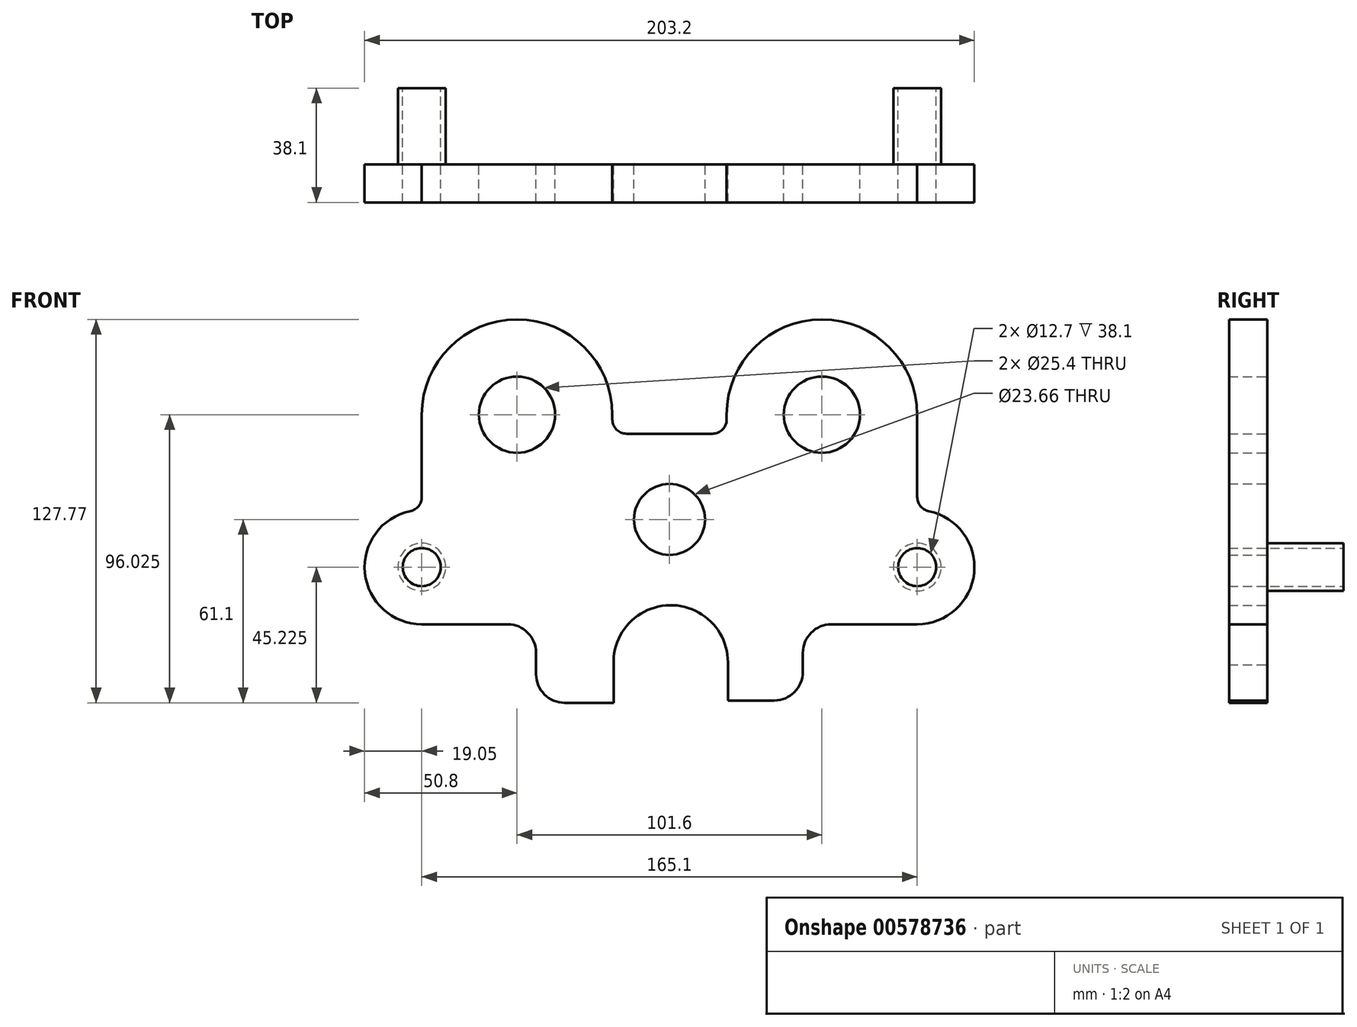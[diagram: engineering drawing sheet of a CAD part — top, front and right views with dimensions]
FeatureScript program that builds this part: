
annotation { "Feature Type Name" : "Feature", "Feature Type Description" : "" }
export const myFeature = defineFeature(function(context is Context, id is Id, definition is map)
    precondition{}
    {
        {
            var Q0;
            Q0=qCreatedBy(makeId("Front.planeOp"),FACE);
            var sketch = newSketch(context, id + "F0", { "sketchPlane" : qUnion([Q0])});
            skArc(sketch, "E0", {"start": v(82.55, 34.93) * mm, "mid": v(50.8, 66.68) * mm, "end": v(19.05, 34.93) * mm});
            skArc(sketch, "E1", {"start": v(-19.05, 34.93) * mm, "mid": v(-50.8, 66.68) * mm, "end": v(-82.55, 34.93) * mm});
            skLineSegment(sketch, "E2", {"start": v(-82.55, 34.92) * mm, "end": v(-82.55, 7.46) * mm});
            skLineSegment(sketch, "E3", {"start": v(82.55, 34.93) * mm, "end": v(82.55, 7.46) * mm});
            skCircle(sketch, "E4", {"center": v(50.8, 34.93) * mm, "radius": 12.7 * mm});
            skCircle(sketch, "E5", {"center": v(-50.8, 34.93) * mm, "radius": 12.7 * mm});
            skLineSegment(sketch, "E6", {"start": v(0, 94.12) * mm, "end": v(0, -101.3) * mm, "construction": true});
            skArc(sketch, "E7", {"start": v(-86.36, 2.8) * mm, "mid": v(-101.5, -17.79) * mm, "end": v(-82.55, -34.92) * mm});
            skArc(sketch, "E8", {"start": v(82.55, -34.92) * mm, "mid": v(101.5, -17.79) * mm, "end": v(86.36, 2.8) * mm});
            skLineSegment(sketch, "E9", {"start": v(82.55, -34.92) * mm, "end": v(53.98, -34.92) * mm});
            skLineSegment(sketch, "E10", {"start": v(-82.55, -34.92) * mm, "end": v(-53.97, -34.92) * mm});
            skLineSegment(sketch, "E11", {"start": v(-44.45, -44.45) * mm, "end": v(-44.45, -51.58) * mm});
            skLineSegment(sketch, "E12", {"start": v(-34.92, -61.1) * mm, "end": v(-18.63, -61.1) * mm});
            skLineSegment(sketch, "E13", {"start": v(44.45, -44.45) * mm, "end": v(44.45, -50.8) * mm});
            skLineSegment(sketch, "E14", {"start": v(34.93, -60.32) * mm, "end": v(19.45, -60.32) * mm});
            skLineSegment(sketch, "E15", {"start": v(-18.63, -61.1) * mm, "end": v(-18.63, -48.4) * mm});
            skLineSegment(sketch, "E16", {"start": v(19.45, -60.33) * mm, "end": v(19.45, -47.62) * mm});
            skArc(sketch, "E17", {"start": v(19.45, -47.62) * mm, "mid": v(0.01, -28.58) * mm, "end": v(-18.63, -48.4) * mm});
            skCircle(sketch, "E18", {"center": v(-82.55, -15.88) * mm, "radius": 6.35 * mm});
            skCircle(sketch, "E19", {"center": v(82.55, -15.87) * mm, "radius": 6.35 * mm});
            skCircle(sketch, "E20", {"center": v(0, 0) * mm, "radius": 11.83 * mm});
            skLineSegment(sketch, "E21", {"start": v(-19.05, 34.92) * mm, "end": v(-19.05, 33.34) * mm});
            skLineSegment(sketch, "E22", {"start": v(19.05, 34.93) * mm, "end": v(19.05, 33.34) * mm});
            skLineSegment(sketch, "E23", {"start": v(-14.29, 28.58) * mm, "end": v(14.29, 28.58) * mm});
            skPoint(sketch, "E24.visualSharp", {"position": v(-19.05, 28.58) * mm});
            skArc(sketch, "E24.filletArc", {"start": v(-19.05, 33.34) * mm, "mid": v(-17.66, 29.97) * mm, "end": v(-14.29, 28.58) * mm});
            skPoint(sketch, "E25.visualSharp", {"position": v(19.05, 28.58) * mm});
            skArc(sketch, "E25.filletArc", {"start": v(14.29, 28.58) * mm, "mid": v(17.66, 29.97) * mm, "end": v(19.05, 33.34) * mm});
            skPoint(sketch, "E26.visualSharp", {"position": v(44.45, -34.92) * mm});
            skArc(sketch, "E26.filletArc", {"start": v(53.98, -34.92) * mm, "mid": v(47.24, -37.71) * mm, "end": v(44.45, -44.45) * mm});
            skPoint(sketch, "E27.visualSharp", {"position": v(44.45, -60.32) * mm});
            skArc(sketch, "E27.filletArc", {"start": v(34.93, -60.32) * mm, "mid": v(41.66, -57.54) * mm, "end": v(44.45, -50.8) * mm});
            skPoint(sketch, "E28.visualSharp", {"position": v(-44.45, -61.1) * mm});
            skArc(sketch, "E28.filletArc", {"start": v(-44.45, -51.58) * mm, "mid": v(-41.66, -58.31) * mm, "end": v(-34.92, -61.1) * mm});
            skPoint(sketch, "E29.visualSharp", {"position": v(-44.45, -34.92) * mm});
            skArc(sketch, "E29.filletArc", {"start": v(-44.45, -44.45) * mm, "mid": v(-47.24, -37.71) * mm, "end": v(-53.97, -34.93) * mm});
            skPoint(sketch, "E30.visualSharp", {"position": v(-82.55, 3.18) * mm});
            skArc(sketch, "E30.filletArc", {"start": v(-86.36, 2.8) * mm, "mid": v(-83.62, 4.44) * mm, "end": v(-82.55, 7.46) * mm});
            skPoint(sketch, "E31.visualSharp", {"position": v(82.55, 3.18) * mm});
            skArc(sketch, "E31.filletArc", {"start": v(82.55, 7.46) * mm, "mid": v(83.62, 4.44) * mm, "end": v(86.36, 2.8) * mm});
            skCircle(sketch, "E32", {"center": v(-82.55, -15.88) * mm, "radius": 7.94 * mm});
            skCircle(sketch, "E33", {"center": v(82.55, -15.87) * mm, "radius": 7.94 * mm});
            skSolve(sketch);
        }
        {
            var Q0;
            Q0 = qSketchRegion(id + "F0", true);
            var Q1;
            Q1=makeQuery(id+"F0.imprint","IMPRINT",FACE,{"disambiguationData":[TD([[makeQuery(id+"F0.imprint","IMPRINT",EDGE,{"derivedFrom":sQuery(id+"F0.wireOp",EDGE,"E18")}),-1.0]])]});
            var Q2;
            Q2=makeQuery(id+"F0.imprint","IMPRINT",FACE,{"disambiguationData":[TD([[makeQuery(id+"F0.imprint","IMPRINT",EDGE,{"derivedFrom":sQuery(id+"F0.wireOp",EDGE,"E19")}),-1.0]])]});
            extrude(context, id + "F1", {"entities" : qUnion([Q0, Q1, Q2]), "depth" : 12.7 * mm, "offsetDistance" : 25.4 * mm});
        }
        {
            var Q0;
            Q0=makeQuery(id+"F0.imprint","IMPRINT",FACE,{"disambiguationData":[TD([[makeQuery(id+"F0.imprint","IMPRINT",EDGE,{"derivedFrom":sQuery(id+"F0.wireOp",EDGE,"E19")}),-1.0]])]});
            extrude(context, id + "F2", {"entities" : qUnion([Q0]), "operationType" : NewBodyOperationType.ADD, "oppositeDirection" : true, "depth" : 25.4 * mm, "offsetDistance" : 25.4 * mm});
        }
        {
            var Q0;
            Q0=makeQuery(id+"F0.imprint","IMPRINT",FACE,{"disambiguationData":[TD([[makeQuery(id+"F0.imprint","IMPRINT",EDGE,{"derivedFrom":sQuery(id+"F0.wireOp",EDGE,"E18")}),-1.0]])]});
            extrude(context, id + "F3", {"entities" : qUnion([Q0]), "operationType" : NewBodyOperationType.ADD, "oppositeDirection" : true, "depth" : 25.4 * mm, "offsetDistance" : 25.4 * mm});
        }
    });
